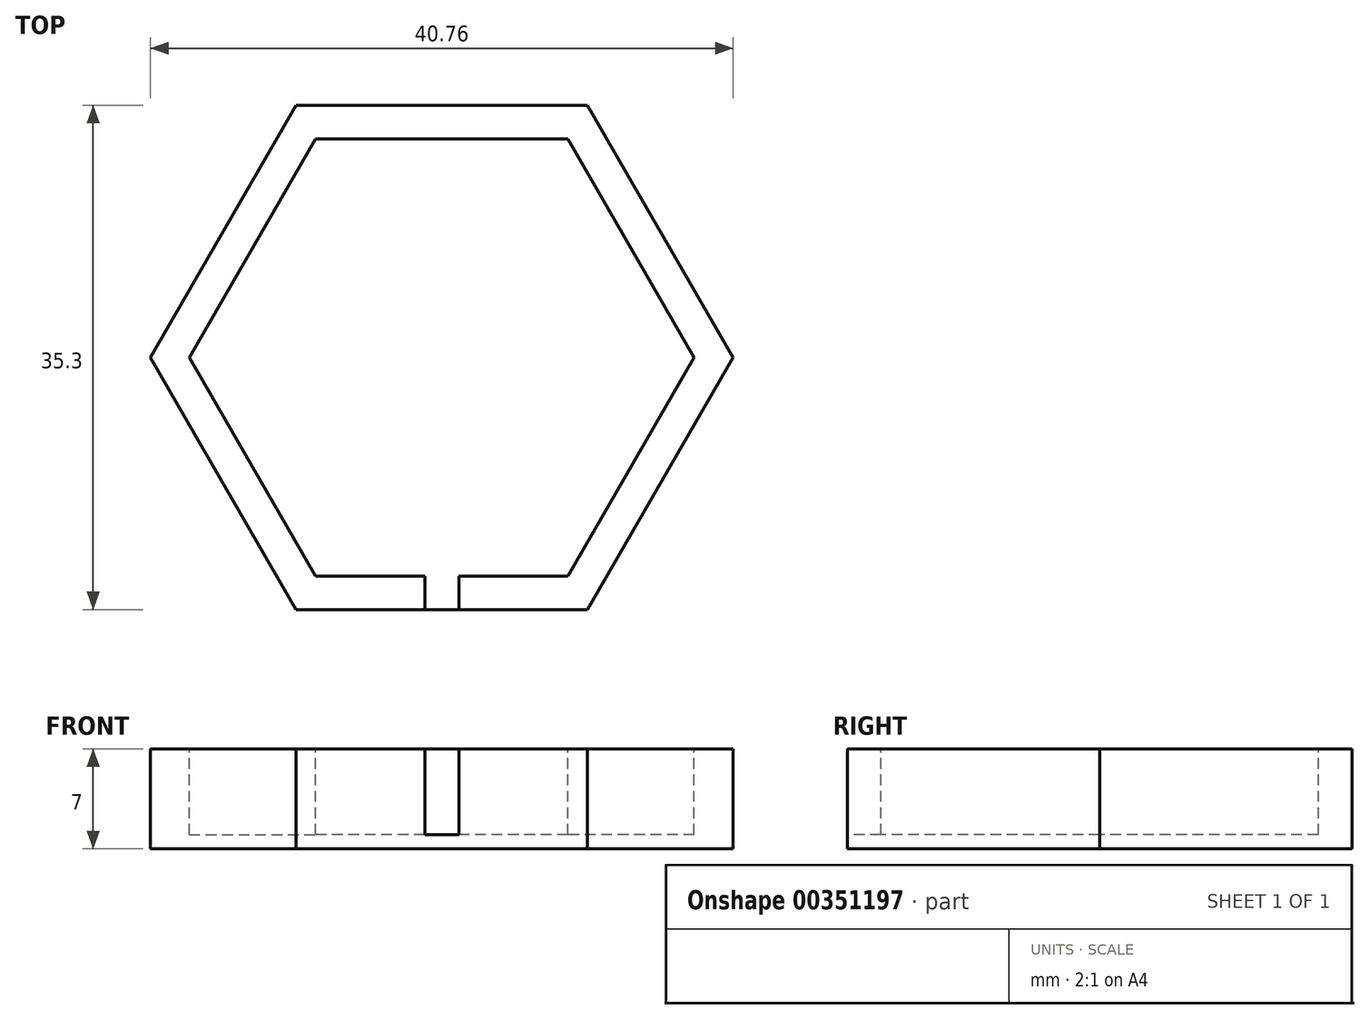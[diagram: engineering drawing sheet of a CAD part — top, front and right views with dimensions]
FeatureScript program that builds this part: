
annotation { "Feature Type Name" : "Feature", "Feature Type Description" : "" }
export const myFeature = defineFeature(function(context is Context, id is Id, definition is map)
    precondition{}
    {
        {
            var Q0;
            Q0=qCreatedBy(makeId("Top.planeOp"),FACE);
            var sketch = newSketch(context, id + "F0", { "sketchPlane" : qUnion([Q0])});
            skCircle(sketch, "E0.cCircle", {"center": v(0, 0) * mm, "radius": 17.65 * mm, "construction": true});
            skLineSegment(sketch, "E0.0", {"start": v(10.19, -17.65) * mm, "end": v(-10.19, -17.65) * mm});
            skLineSegment(sketch, "E0.1", {"start": v(-10.19, -17.65) * mm, "end": v(-20.38, 0) * mm});
            skLineSegment(sketch, "E0.2", {"start": v(-20.38, 0) * mm, "end": v(-10.19, 17.65) * mm});
            skLineSegment(sketch, "E0.3", {"start": v(-10.19, 17.65) * mm, "end": v(10.19, 17.65) * mm});
            skLineSegment(sketch, "E0.4", {"start": v(10.19, 17.65) * mm, "end": v(20.38, 0) * mm});
            skLineSegment(sketch, "E0.5", {"start": v(20.38, 0) * mm, "end": v(10.19, -17.65) * mm});
            skPoint(sketch, "E0.0.midPoint", {"position": v(0, -17.65) * mm});
            skSolve(sketch);
        }
        {
            var Q0;
            Q0 = qSketchRegion(id + "F0", true);
            extrude(context, id + "F1", {"entities" : qUnion([Q0]), "depth" : 7 * mm});
        }
        {
            var Q0;
            Q0=makeQuery(id+"F1.opExtrude","CAP_FACE",FACE,{"disambiguationData":[OSD([sQuery(id+"F0.wireOp",EDGE,"E0.0"),sQuery(id+"F0.wireOp",EDGE,"E0.1"),sQuery(id+"F0.wireOp",EDGE,"E0.2"),sQuery(id+"F0.wireOp",EDGE,"E0.3"),sQuery(id+"F0.wireOp",EDGE,"E0.4"),sQuery(id+"F0.wireOp",EDGE,"E0.5")])],"isStart":false});
            var sketch = newSketch(context, id + "F2", { "sketchPlane" : qUnion([Q0])});
            skCircle(sketch, "E1.cCircle", {"center": v(0, 0) * mm, "radius": 15.3 * mm, "construction": true});
            skPoint(sketch, "E1.cCircle.perimeterSnap0", {"position": v(0, -17.65) * mm});
            skLineSegment(sketch, "E1.0", {"start": v(8.83, -15.3) * mm, "end": v(-8.83, -15.3) * mm});
            skLineSegment(sketch, "E1.1", {"start": v(-8.83, -15.3) * mm, "end": v(-17.66, 0) * mm});
            skLineSegment(sketch, "E1.2", {"start": v(-17.66, 0) * mm, "end": v(-8.83, 15.3) * mm});
            skLineSegment(sketch, "E1.3", {"start": v(-8.83, 15.3) * mm, "end": v(8.83, 15.3) * mm});
            skLineSegment(sketch, "E1.4", {"start": v(8.83, 15.3) * mm, "end": v(17.66, 0) * mm});
            skLineSegment(sketch, "E1.5", {"start": v(17.66, 0) * mm, "end": v(8.83, -15.3) * mm});
            skPoint(sketch, "E1.0.midPoint", {"position": v(0, -15.3) * mm});
            skPoint(sketch, "E1.0.midPoint.positionSnap0", {"position": v(0, -17.65) * mm});
            skSolve(sketch);
        }
        {
            var Q0;
            Q0 = qSketchRegion(id + "F2", true);
            extrude(context, id + "F3", {"entities" : qUnion([Q0]), "operationType" : NewBodyOperationType.REMOVE, "oppositeDirection" : true, "depth" : 6 * mm});
        }
        {
            var Q0;
            Q0=makeQuery(id+"F1.opExtrude","CAP_FACE",FACE,{"disambiguationData":[OSD([sQuery(id+"F0.wireOp",EDGE,"E0.0"),sQuery(id+"F0.wireOp",EDGE,"E0.1"),sQuery(id+"F0.wireOp",EDGE,"E0.2"),sQuery(id+"F0.wireOp",EDGE,"E0.3"),sQuery(id+"F0.wireOp",EDGE,"E0.4"),sQuery(id+"F0.wireOp",EDGE,"E0.5")])],"isStart":false});
            var sketch = newSketch(context, id + "F4", { "sketchPlane" : qUnion([Q0])});
            skLineSegment(sketch, "E2.bottom", {"start": v(-1.18, -15.3) * mm, "end": v(1.21, -15.3) * mm});
            skLineSegment(sketch, "E2.top", {"start": v(-1.18, -17.65) * mm, "end": v(1.21, -17.65) * mm});
            skLineSegment(sketch, "E2.left", {"start": v(-1.18, -15.3) * mm, "end": v(-1.18, -17.65) * mm});
            skLineSegment(sketch, "E2.right", {"start": v(1.21, -15.3) * mm, "end": v(1.21, -17.65) * mm});
            skSolve(sketch);
        }
        {
            var Q0;
            Q0 = qSketchRegion(id + "F4", true);
            extrude(context, id + "F5", {"entities" : qUnion([Q0]), "operationType" : NewBodyOperationType.REMOVE, "oppositeDirection" : true, "depth" : 6 * mm});
        }
    });
